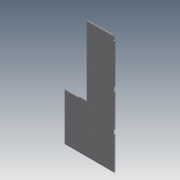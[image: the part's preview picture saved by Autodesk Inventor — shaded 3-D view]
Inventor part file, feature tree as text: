
AUTODESK INVENTOR PART (.ipt)
format: ipt  version: 2011 (Build 150239000, 239)  size: 886,784 bytes
history: native  units: in
note: dims shown in document units (in); Inventor stores cm internally (conversion verified against a paired STEP export)
features: sketch x41, extrude x40
ambient origin geometry x8: Origin, YZ Plane, XZ Plane, XY Plane, X Axis, Y Axis, Z Axis, Center Point
bodies: Solid1 (feature_tree)
feature tree (81):
  extrude  "Extrusion1"  Depth=35.0in
  extrude  "Extrusion2"  Depth=0.25in
  extrude  "Extrusion3"  Depth=2.0in
  extrude  "Extrusion4"  Depth=2.0in
  extrude  "Extrusion5"  Depth=2.0in
  extrude  "Extrusion6"  Depth=2.0in
  extrude  "Extrusion7"  Depth=2.0in
  extrude  "Extrusion8"  Depth=2.0in
  extrude  "Extrusion9"  Depth=2.0in
  extrude  "Extrusion10"  Depth=2.0in
  extrude  "Extrusion11"  Depth=0.25in TaperAngle=0.0deg
  sketch  "Sketch12"  dims[d24=0.25in d25=0.25in d26=0.0in]
  extrude  "Extrusion12"  Depth=0.25in TaperAngle=0.0deg
  extrude  "Extrusion13"  Depth=0.25in
  extrude  "Extrusion14"  Depth=2.0in
  extrude  "Extrusion15"  Depth=1.0in
  extrude  "Extrusion16"  Depth=2.0in
  extrude  "Extrusion17"  Depth=1.0in TaperAngle=0.0deg
  extrude  "Extrusion18"  Depth=1.0in TaperAngle=0.0deg
  extrude  "Extrusion19"  Depth=1.0in TaperAngle=0.0deg
  extrude  "Extrusion20"  Depth=1.75in
  extrude  "Extrusion21"  Depth=1.75in
  extrude  "Extrusion22"  Depth=0.156in
  extrude  "Extrusion23"  Depth=0.25in TaperAngle=0.0deg
  extrude  "Extrusion24"  Depth=0.25in
  extrude  "Extrusion25"  Depth=0.25in
  extrude  "Extrusion26"  Depth=0.156in
  extrude  "Extrusion27"  Depth=0.25in
  extrude  "Extrusion28"  Depth=10.35in
  extrude  "Extrusion29"  Depth=1.0in TaperAngle=0.0deg
  extrude  "Extrusion30"  Depth=1.0in TaperAngle=0.0deg
  extrude  "Extrusion31"  Depth=1.0in TaperAngle=0.0deg
  extrude  "Extrusion32"  Depth=0.25in TaperAngle=0.0deg
  extrude  "Extrusion33"  Depth=5.75in
  extrude  "Extrusion34"  Depth=31.14in
  extrude  "Extrusion35"  Depth=1.0in TaperAngle=0.0deg
  extrude  "Extrusion36"  Depth=0.25in
  extrude  "Extrusion37"  Depth=0.25in
  extrude  "Extrusion38"  Depth=0.25in TaperAngle=0.0deg
  extrude  "Extrusion39"  Depth=0.25in TaperAngle=0.0deg
  extrude  "Extrusion40"  Depth=0.25in TaperAngle=0.0deg
  sketch  "Sketch1"  dims[d0=12.85in d1=35.0in]
  sketch  "Sketch2"  dims[d2=0.25in d3=0.0in d4=0.25in]
  sketch  "Sketch3"  dims[d5=2.0in d6=2.0in]
  sketch  "Sketch4"  dims[d7=2.0in d8=2.0in]
  sketch  "Sketch5"  dims[d9=2.0in d10=2.0in]
  sketch  "Sketch6"  dims[d11=2.0in d12=2.0in]
  sketch  "Sketch7"  dims[d13=2.0in d14=2.0in]
  sketch  "Sketch8"  dims[d15=2.0in d16=2.0in]
  sketch  "Sketch9"  dims[d17=2.0in d18=2.0in]
  sketch  "Sketch10"  dims[d19=2.0in d20=2.0in]
  sketch  "Sketch11"  dims[d21=2.0in d22=0.25in d23=0.0in]
  sketch  "Sketch13"  dims[d27=6.175in d28=0.25in]
  sketch  "Sketch14"  dims[d29=1.0in d30=2.0in]
  sketch  "Sketch15"  dims[d31=2.0in d32=1.0in]
  sketch  "Sketch16"  dims[d33=2.0in d34=2.0in]
  sketch  "Sketch17"  dims[d35=0.25in d36=0.0in d37=1.0in d38=0.0in]
  sketch  "Sketch18"  dims[d39=1.0in d40=0.0in d41=1.0in d42=0.0in]
  sketch  "Sketch19"  dims[d43=0.25in d44=1.0in d45=0.0in]
  sketch  "Sketch20"  dims[d46=0.5in d47=1.75in]
  sketch  "Sketch21"  dims[d48=0.5in d49=1.75in]
  sketch  "Sketch22"  dims[d50=0.156in d51=0.156in]
  sketch  "Sketch23"  dims[d52=1.0in d53=0.0in d54=0.25in d55=0.0in]
  sketch  "Sketch24"  dims[d56=0.25in d57=0.0in d58=0.25in]
  sketch  "Sketch25"  dims[d59=1.75in d60=0.25in]
  sketch  "Sketch26"  dims[d61=0.156in d62=0.156in]
  sketch  "Sketch27"  dims[d63=0.25in d64=0.0in d65=0.25in]
  sketch  "Sketch28"  dims[d66=1.0in d67=10.35in]
  sketch  "Sketch29"  dims[d68=0.25in d69=1.0in d70=0.0in]
  sketch  "Sketch30"  dims[d71=0.25in d72=0.0in d73=1.0in d74=0.0in]
  sketch  "Sketch31"  dims[d75=1.0in d76=0.0in d77=1.0in d78=0.0in]
  sketch  "Sketch32"  dims[d79=0.25in d80=0.0in d81=0.25in d82=0.0in]
  sketch  "Sketch33"  dims[d83=12.25in d84=5.75in]
  sketch  "Sketch34"  dims[d85=1.0in d86=0.0in d87=31.14in]
  sketch  "Sketch35"  dims[d88=0.25in d89=1.0in d90=0.0in]
  sketch  "Sketch36"  dims[d91=1.0in d92=0.0in d93=0.25in]
  sketch  "Sketch37"  dims[d94=1.0in d95=0.0in d96=0.25in]
  sketch  "Sketch38"  dims[d97=0.24in d98=0.25in d99=0.0in]
  sketch  "Sketch39"  dims[d100=0.25in d101=0.25in d102=0.0in]
  sketch  "Sketch40"  dims[d103=0.25in d104=0.25in d105=0.0in]
  sketch  "Sketch41"  dims[d106=0.25in d107=0.25in d108=0.0in d109=0.25in d110=1.0in d111=0.0in d112=3.25in d113=0.25in d114=1.0in d115=0.0in d116=0.75in d117=1.0in d118=0.0in d119=9.5in d120=0.25in d121=0.5in d122=0.25in d123=1.0in d124=0.0in d125=0.5in d126=1.0in d127=0.0in d128=8.25in d129=1.0in d130=0.25in d131=1.0in d132=0.0in d133=0.25in d134=1.0in d135=1.0in d136=0.0in d137=0.25in d138=0.0in d139=4.912in d140=5.603in d141=0.185in d142=0.25in d143=0.0in d144=5.418in d145=8.593in d146=0.185in d147=0.185in d148=0.25in d149=0.0in d150=0.5in d151=0.5in d152=1.0in d153=0.0in d154=3.5in d155=0.25in d156=1.0in d157=0.0in d158=1.0in d159=2.0in d160=0.25in d161=0.0in]
